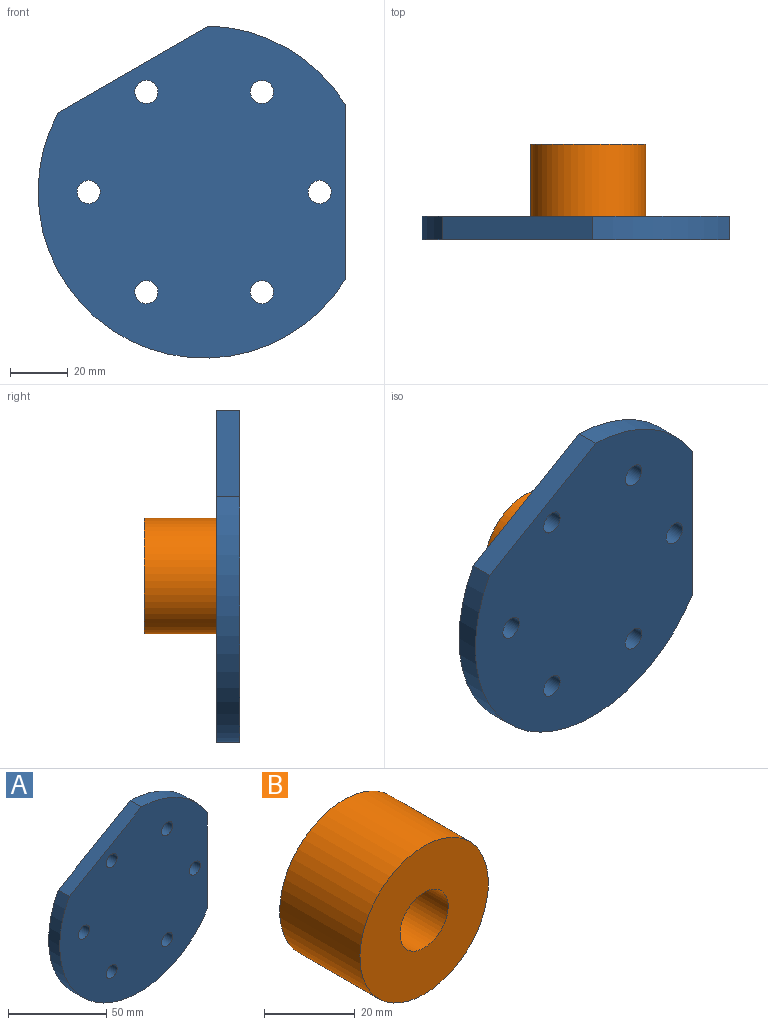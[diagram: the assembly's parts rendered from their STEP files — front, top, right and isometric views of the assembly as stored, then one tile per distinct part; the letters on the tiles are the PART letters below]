
ASSEMBLY  parts=2 mates=1
PART A: 12 faces, bbox 106.6x8x115 mm
  f0: cylinder r=57.5mm len=47.62mm, axis (0,1,0), area 458.8mm2, adj f1,f8,f10,f11
  f1: plane 51.96x30mm, normal (-0.5,0,0.87), area 480mm2, adj f0,f2,f10,f11
  f2: cylinder r=57.5mm len=106.58mm, axis (0,1,0), area 1422.2mm2, adj f1,f8,f10,f11
  f3: cylinder r=4mm len=8mm, axis (0,1,0), area 201.1mm2, adj f10,f11
  f4: cylinder r=4mm len=8mm, axis (0,1,0), area 201.1mm2, adj f10,f11
  f5: cylinder r=4mm len=8mm, axis (0,1,0), area 201.1mm2, adj f10,f11
  f6: cylinder r=4mm len=8mm, axis (0,1,0), area 201.1mm2, adj f10,f11
  f7: cylinder r=4mm len=8mm, axis (0,1,0), area 201.1mm2, adj f10,f11
  f8: plane 59.92x8mm, normal (1,0,0), area 479.4mm2, adj f0,f2,f10,f11
  f9: cylinder r=4mm len=8mm, axis (0,1,0), area 201.1mm2, adj f10,f11
  f10: plane 114.98x106.58mm, normal (0,-1,0), area 9400.5mm2, adj f0,f1,f2,f3,f4,f5,f6,f7
  f11: plane 114.98x106.58mm, normal (0,1,0), area 9400.5mm2, adj f0,f1,f2,f3,f4,f5,f6,f7
PART B: 4 faces, bbox 40x25x40 mm
  f0: cylinder r=7.5mm len=25mm, axis (0,1,0), area 1178.1mm2, adj f2,f3
  f1: cylinder r=20mm len=40mm, axis (0,1,0), area 3141.6mm2, adj f2,f3
  f2: plane 40x40mm, normal (0,-1,0), area 1079.9mm2, adj f0,f1
  f3: plane 40x40mm, normal (0,1,0), area 1079.9mm2, adj f0,f1
PLACE A t=(51.81,-44.35,43.83)mm
PLACE B t=(-122.81,-19.35,37.49)mm
MATE planar B.f1 <-> A.f0  axis (0,-1,0) through (-122.81,-44.35,37.49)mm
